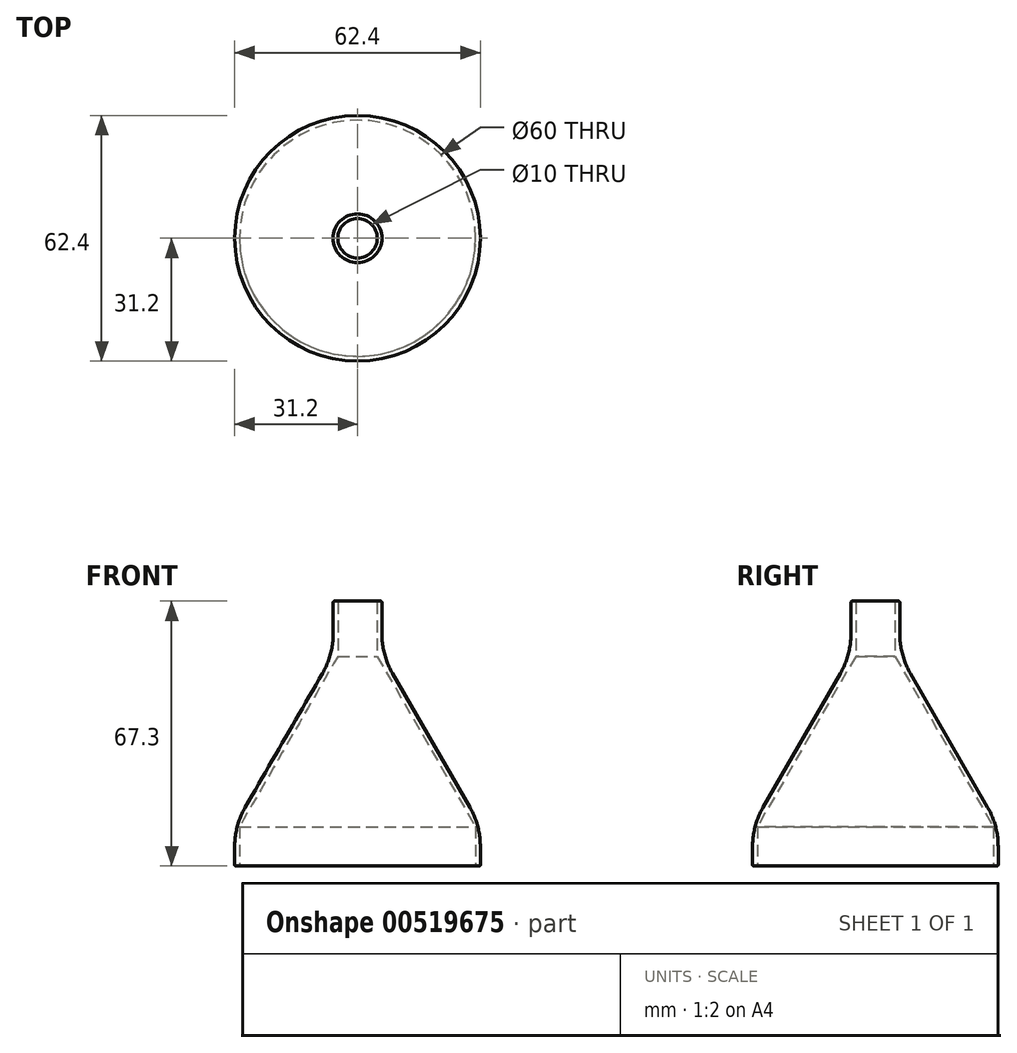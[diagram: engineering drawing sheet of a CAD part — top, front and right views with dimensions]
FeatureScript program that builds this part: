
annotation { "Feature Type Name" : "Feature", "Feature Type Description" : "" }
export const myFeature = defineFeature(function(context is Context, id is Id, definition is map)
    precondition{}
    {
        {
            var Q0;
            Q0=qCreatedBy(makeId("Front.planeOp"),FACE);
            var sketch = newSketch(context, id + "F0", { "sketchPlane" : qUnion([Q0])});
            skLineSegment(sketch, "E0", {"start": v(0, -39.72) * mm, "end": v(0, 56.13) * mm, "construction": true});
            skLineSegment(sketch, "E1", {"start": v(-30, 0) * mm, "end": v(-30, 10) * mm});
            skLineSegment(sketch, "E2", {"start": v(-30, 10) * mm, "end": v(-5, 53.3) * mm});
            skLineSegment(sketch, "E3", {"start": v(-5, 53.3) * mm, "end": v(-5, 67.3) * mm});
            skLineSegment(sketch, "E4.0", {"start": v(-6.2, 53.62) * mm, "end": v(-6.2, 67.3) * mm});
            skLineSegment(sketch, "E4.1", {"start": v(-31.2, 10.32) * mm, "end": v(-6.2, 53.62) * mm});
            skLineSegment(sketch, "E4.2", {"start": v(-31.2, 0) * mm, "end": v(-31.2, 10.32) * mm});
            skLineSegment(sketch, "E5", {"start": v(-6.2, 67.3) * mm, "end": v(-5, 67.3) * mm});
            skLineSegment(sketch, "E6", {"start": v(-31.2, 0) * mm, "end": v(-30, 0) * mm});
            skSolve(sketch);
        }
        {
            var Q0;
            Q0=makeQuery(id+"F0.imprint","IMPRINT",FACE,{"disambiguationData":[TD([[makeQuery(id+"F0.imprint","IMPRINT",EDGE,{"derivedFrom":sQuery(id+"F0.wireOp",EDGE,"E1")}),1.0]])]});
            var Q1;
            Q1=sQuery(id+"F0.wireOp",EDGE,"E0");
            revolve(context, id + "F1", {"entities" : qUnion([Q0]), "axis" : qUnion([Q1]), "revolveType" : RevolveType.FULL});
        }
        {
            var Q0;
            Q0=makeQuery(id+"F1.opRevolve","SWEPT_EDGE",EDGE,{"disambiguationData":[OSD([sQuery(id+"F0.wireOp",EDGE,"E4.1"),sQuery(id+"F0.wireOp",EDGE,"E4.2")])]});
            var Q1;
            Q1=makeQuery(id+"F1.opRevolve","SWEPT_EDGE",EDGE,{"disambiguationData":[OSD([sQuery(id+"F0.wireOp",EDGE,"E4.0"),sQuery(id+"F0.wireOp",EDGE,"E4.1")])]});
            fillet(context, id + "F2", {"entities" : qUnion([Q0, Q1]), "radius" : 20 * mm, "tangentPropagation" : true, "allowEdgeOverflow" : false});
        }
        {
            var Q0;
            Q0=makeQuery(id+"F1.opRevolve","SWEPT_FACE",FACE,{"disambiguationData":[OSD([sQuery(id+"F0.wireOp",EDGE,"E5")])]});
            fillet(context, id + "F3", {"entities" : qUnion([Q0]), "radius" : .3 * mm, "tangentPropagation" : true, "allowEdgeOverflow" : false});
        }
        {
            var Q0;
            Q0=makeQuery(id+"F1.opRevolve","SWEPT_FACE",FACE,{"disambiguationData":[OSD([sQuery(id+"F0.wireOp",EDGE,"E6")])]});
            fillet(context, id + "F4", {"entities" : qUnion([Q0]), "radius" : .3 * mm, "tangentPropagation" : true, "allowEdgeOverflow" : false});
        }
    });
